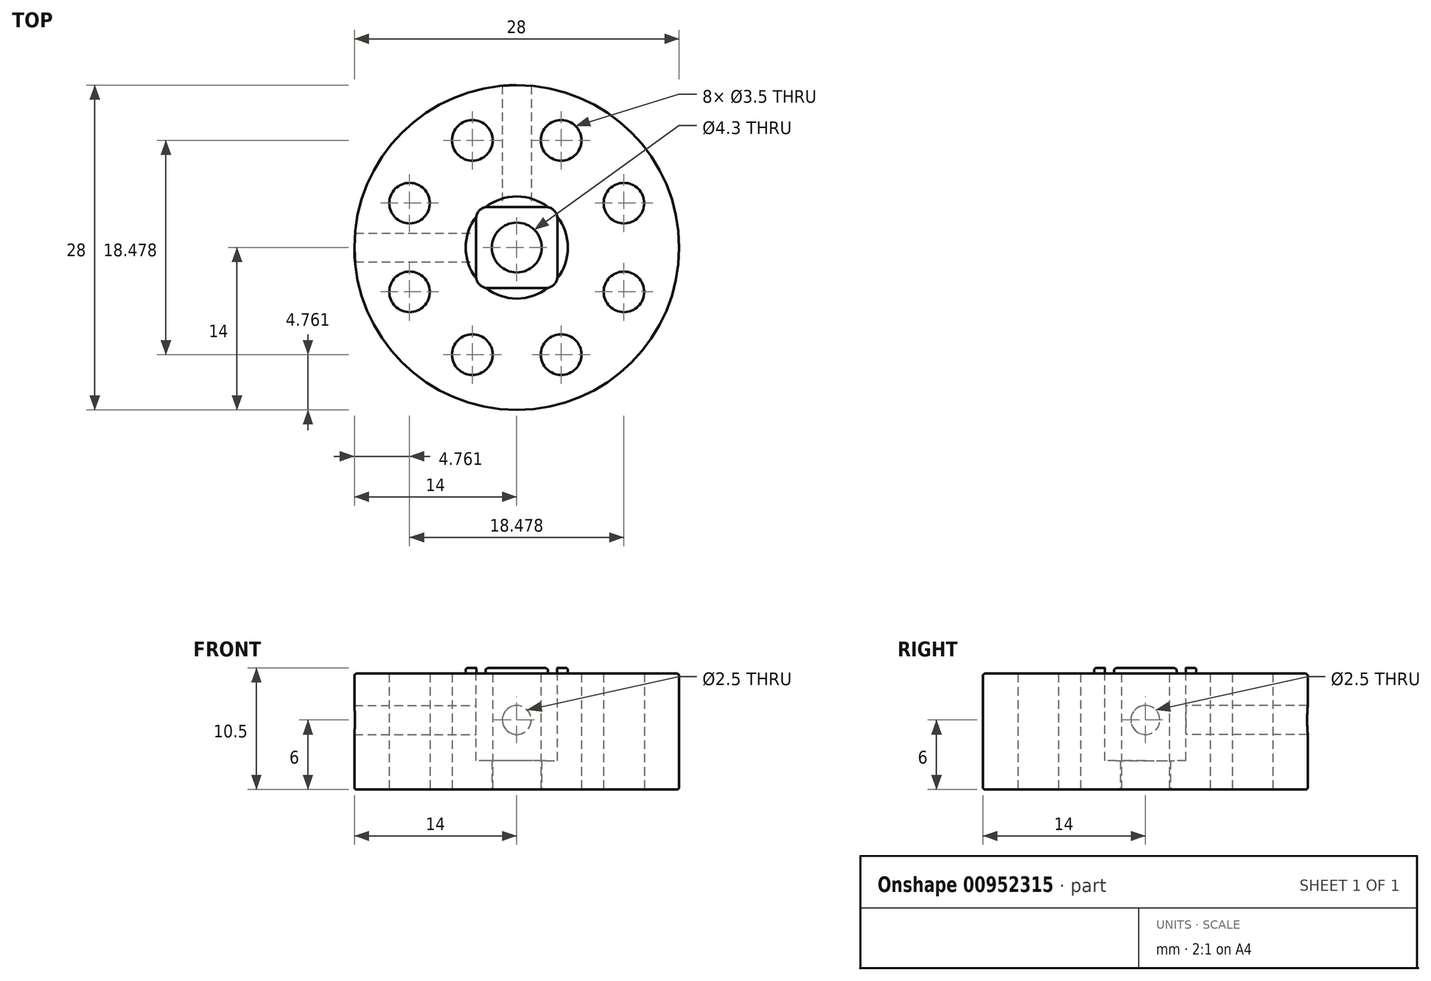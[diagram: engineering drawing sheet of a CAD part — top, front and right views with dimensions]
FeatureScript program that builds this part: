
annotation { "Feature Type Name" : "Feature", "Feature Type Description" : "" }
export const myFeature = defineFeature(function(context is Context, id is Id, definition is map)
    precondition{}
    {
        {
            var Q0;
            Q0=qCreatedBy(makeId("Top.planeOp"),FACE);
            var sketch = newSketch(context, id + "F0", { "sketchPlane" : qUnion([Q0])});
            skCircle(sketch, "E0", {"center": v(0, 0) * mm, "radius": 14 * mm});
            skSolve(sketch);
        }
        {
            var Q0;
            Q0=qSketchRegion(id+"F0",true);
            extrude(context, id + "F1", {"entities" : qUnion([Q0]), "depth" : 10 * mm, "offsetDistance" : 25 * mm});
        }
        {
            var Q0;
            Q0=makeQuery(id+"F1.opExtrude","CAP_FACE",FACE,{"disambiguationData":[OSD([sQuery(id+"F0.wireOp",EDGE,"E0")])],"isStart":false});
            var sketch = newSketch(context, id + "F2", { "sketchPlane" : qUnion([Q0])});
            skCircle(sketch, "E1", {"center": v(0, 0) * mm, "radius": 4.4 * mm});
            skSolve(sketch);
        }
        {
            var Q0;
            {var subQ0=sQuery(id+"F2.wireOp",EDGE,"q5Iyk92a-tP6P-DxR0-Fjeh-1lhmU1jtPTMJ");var subQ1=makeQuery(id+"F5.boolean.opBoolean","COPY",EDGE,{"derivedFrom":makeQuery(id+"F5.opExtrude","CAP_EDGE",EDGE,{"disambiguationData":[OSD([sQuery(id+"F4.wireOp",EDGE,"E2.bottom")])],"isStart":true})});var subQ2=makeQuery(id+"F2.imprint","INTERSECT",VERTEX,{"disambiguationData":[OD(0.0)],"derivedFrom":[subQ1,subQ0]});Q0=makeQuery(id+"F2.imprint","IMPRINT",FACE,{"disambiguationData":[TD([[makeQuery(id+"F2.imprint","IMPRINT",EDGE,{"disambiguationData":[TD([[subQ2,-1.0]])],"derivedFrom":subQ0}),1.0]])]});}
            var Q1;
            {var subQ0=sQuery(id+"F2.wireOp",EDGE,"q5Iyk92a-tP6P-DxR0-Fjeh-1lhmU1jtPTMJ");var subQ1=makeQuery(id+"F5.boolean.opBoolean","COPY",EDGE,{"derivedFrom":makeQuery(id+"F5.opExtrude","CAP_EDGE",EDGE,{"disambiguationData":[OSD([sQuery(id+"F4.wireOp",EDGE,"E2.right")])],"isStart":true})});var subQ2=makeQuery(id+"F2.imprint","INTERSECT",VERTEX,{"disambiguationData":[OD(0.0)],"derivedFrom":[subQ1,subQ0]});Q1=makeQuery(id+"F2.imprint","IMPRINT",FACE,{"disambiguationData":[TD([[makeQuery(id+"F2.imprint","IMPRINT",EDGE,{"disambiguationData":[TD([[subQ2,-1.0]])],"derivedFrom":subQ0}),1.0]])]});}
            var Q2;
            {var subQ0=sQuery(id+"F2.wireOp",EDGE,"q5Iyk92a-tP6P-DxR0-Fjeh-1lhmU1jtPTMJ");var subQ1=makeQuery(id+"F5.boolean.opBoolean","COPY",EDGE,{"derivedFrom":makeQuery(id+"F5.opExtrude","CAP_EDGE",EDGE,{"disambiguationData":[OSD([sQuery(id+"F4.wireOp",EDGE,"E2.top")])],"isStart":true})});var subQ2=makeQuery(id+"F2.imprint","INTERSECT",VERTEX,{"disambiguationData":[OD(0.0)],"derivedFrom":[subQ1,subQ0]});Q2=makeQuery(id+"F2.imprint","IMPRINT",FACE,{"disambiguationData":[TD([[makeQuery(id+"F2.imprint","IMPRINT",EDGE,{"disambiguationData":[TD([[subQ2,-1.0]])],"derivedFrom":subQ0}),1.0]])]});}
            var Q3;
            {var subQ0=sQuery(id+"F2.wireOp",EDGE,"q5Iyk92a-tP6P-DxR0-Fjeh-1lhmU1jtPTMJ");var subQ1=makeQuery(id+"F5.boolean.opBoolean","COPY",EDGE,{"derivedFrom":makeQuery(id+"F5.opExtrude","CAP_EDGE",EDGE,{"disambiguationData":[OSD([sQuery(id+"F4.wireOp",EDGE,"E2.left")])],"isStart":true})});var subQ2=makeQuery(id+"F2.imprint","INTERSECT",VERTEX,{"disambiguationData":[OD(0.0)],"derivedFrom":[subQ1,subQ0]});Q3=makeQuery(id+"F2.imprint","IMPRINT",FACE,{"disambiguationData":[TD([[makeQuery(id+"F2.imprint","IMPRINT",EDGE,{"disambiguationData":[TD([[subQ2,1.0]])],"derivedFrom":subQ0}),1.0]])]});}
            var Q4;
            Q4=makeQuery(id+"F2.imprint","IMPRINT",FACE,{"disambiguationData":[TD([[makeQuery(id+"F2.imprint","IMPRINT",EDGE,{"derivedFrom":sQuery(id+"F2.wireOp",EDGE,"E1")}),1.0]])]});
            extrude(context, id + "F3", {"entities" : qUnion([Q0, Q1, Q2, Q3, Q4]), "operationType" : NewBodyOperationType.ADD, "depth" : 0.5 * mm, "offsetDistance" : 25 * mm});
        }
        {
            var Q0;
            Q0=makeQuery(id+"F3.opExtrude","CAP_FACE",FACE,{"disambiguationData":[OSD([sQuery(id+"F2.wireOp",EDGE,"E1")])],"isStart":false});
            var sketch = newSketch(context, id + "F4", { "sketchPlane" : qUnion([Q0])});
            skLineSegment(sketch, "E2.bottom", {"start": v(3.5, -3.5) * mm, "end": v(-3.5, -3.5) * mm});
            skLineSegment(sketch, "E2.top", {"start": v(3.5, 3.5) * mm, "end": v(-3.5, 3.5) * mm});
            skLineSegment(sketch, "E2.left", {"start": v(3.5, -3.5) * mm, "end": v(3.5, 3.5) * mm});
            skLineSegment(sketch, "E2.right", {"start": v(-3.5, -3.5) * mm, "end": v(-3.5, 3.5) * mm});
            skPoint(sketch, "E2.middle", {"position": v(0, 0) * mm});
            skSolve(sketch);
        }
        {
            var Q0;
            Q0=qSketchRegion(id+"F4",true);
            extrude(context, id + "F5", {"entities" : qUnion([Q0]), "operationType" : NewBodyOperationType.REMOVE, "oppositeDirection" : true, "depth" : 8 * mm, "offsetDistance" : 25 * mm});
        }
        {
            var Q0;
            Q0=makeQuery(id+"F1.opExtrude","CAP_FACE",FACE,{"disambiguationData":[OSD([sQuery(id+"F0.wireOp",EDGE,"E0")])],"isStart":true});
            var sketch = newSketch(context, id + "F6", { "sketchPlane" : qUnion([Q0])});
            skCircle(sketch, "E3", {"center": v(0, 0) * mm, "radius": 2.15 * mm});
            skSolve(sketch);
        }
        {
            var Q0;
            Q0=qSketchRegion(id+"F6",true);
            var Q1;
            Q1=makeQuery(id+"F5.boolean.opBoolean","COPY",FACE,{"derivedFrom":makeQuery(id+"F5.opExtrude","CAP_FACE",FACE,{"disambiguationData":[OSD([sQuery(id+"F4.wireOp",EDGE,"E2.bottom"),sQuery(id+"F4.wireOp",EDGE,"E2.top"),sQuery(id+"F4.wireOp",EDGE,"E2.left"),sQuery(id+"F4.wireOp",EDGE,"E2.right")])],"isStart":false})});
            extrude(context, id + "F7", {"entities" : qUnion([Q0]), "operationType" : NewBodyOperationType.REMOVE, "endBound" : BoundingType.UP_TO_SURFACE, "oppositeDirection" : true, "depth" : 25 * mm, "endBoundEntityFace" : qUnion([Q1]), "offsetDistance" : 25 * mm});
        }
        {
            var Q0;
            Q0=makeQuery(id+"F1.opExtrude","CAP_FACE",FACE,{"disambiguationData":[OSD([sQuery(id+"F0.wireOp",EDGE,"E0")])],"isStart":true});
            var sketch = newSketch(context, id + "F8", { "sketchPlane" : qUnion([Q0])});
            skCircle(sketch, "E4", {"center": v(9.24, 3.83) * mm, "radius": 1.75 * mm});
            skCircle(sketch, "E5.1.0", {"center": v(3.83, 9.24) * mm, "radius": 1.75 * mm});
            skCircle(sketch, "E5.2.0", {"center": v(-3.83, 9.24) * mm, "radius": 1.75 * mm});
            skCircle(sketch, "E5.3.0", {"center": v(-9.24, 3.83) * mm, "radius": 1.75 * mm});
            skCircle(sketch, "E5.4.0", {"center": v(-9.24, -3.83) * mm, "radius": 1.75 * mm});
            skCircle(sketch, "E5.5.0", {"center": v(-3.83, -9.24) * mm, "radius": 1.75 * mm});
            skCircle(sketch, "E5.6.0", {"center": v(3.83, -9.24) * mm, "radius": 1.75 * mm});
            skCircle(sketch, "E5.7.0", {"center": v(9.24, -3.83) * mm, "radius": 1.75 * mm});
            skPoint(sketch, "E5.center", {"position": v(0, 0) * mm});
            skLineSegment(sketch, "E6", {"start": v(9.24, 3.83) * mm, "end": v(0, 0) * mm});
            skSolve(sketch);
        }
        {
            var Q0;
            Q0=qSketchRegion(id+"F8",true);
            var Q1;
            Q1=makeQuery(id+"F1.opExtrude","CAP_FACE",FACE,{"disambiguationData":[OSD([sQuery(id+"F0.wireOp",EDGE,"E0")])],"isStart":false});
            extrude(context, id + "F9", {"entities" : qUnion([Q0]), "operationType" : NewBodyOperationType.REMOVE, "endBound" : BoundingType.UP_TO_SURFACE, "oppositeDirection" : true, "depth" : 25 * mm, "endBoundEntityFace" : qUnion([Q1]), "offsetDistance" : 25 * mm});
        }
        {
            var Q0;
            Q0=qCreatedBy(makeId("Front.planeOp"),FACE);
            var sketch = newSketch(context, id + "F10", { "sketchPlane" : qUnion([Q0])});
            skCircle(sketch, "E7", {"center": v(0, 6) * mm, "radius": 1.25 * mm});
            skSolve(sketch);
        }
        {
            var Q0;
            Q0=qSketchRegion(id+"F10",true);
            extrude(context, id + "F11", {"entities" : qUnion([Q0]), "operationType" : NewBodyOperationType.REMOVE, "oppositeDirection" : true, "depth" : 25 * mm, "offsetDistance" : 25 * mm});
        }
        {
            var Q0;
            Q0=qCreatedBy(makeId("Right.planeOp"),FACE);
            var sketch = newSketch(context, id + "F12", { "sketchPlane" : qUnion([Q0])});
            skCircle(sketch, "E8", {"center": v(0, 6) * mm, "radius": 1.25 * mm});
            skSolve(sketch);
        }
        {
            var Q0;
            Q0=qSketchRegion(id+"F12",true);
            extrude(context, id + "F13", {"entities" : qUnion([Q0]), "operationType" : NewBodyOperationType.REMOVE, "oppositeDirection" : true, "depth" : 25 * mm, "offsetDistance" : 25 * mm});
        }
        {
            var Q0;
            {var subQ0=sQuery(id+"F4.wireOp",EDGE,"E2.right");var subQ1=sQuery(id+"F4.wireOp",EDGE,"E2.bottom");Q0=makeQuery(id+"F3.boolean.opBoolean","MERGE",EDGE,{"derivedFrom":[makeQuery(id+"F5.boolean.opBoolean","COPY",EDGE,{"derivedFrom":makeQuery(id+"F5.opExtrude","SWEPT_EDGE",EDGE,{"disambiguationData":[OSD([subQ1,subQ0])]})}),makeQuery(id+"F3.opExtrude","SWEPT_EDGE",EDGE,{"disambiguationData":[OSD([subQ1,subQ0])]})]});}
            var Q1;
            {var subQ0=sQuery(id+"F4.wireOp",EDGE,"E2.left");var subQ1=sQuery(id+"F4.wireOp",EDGE,"E2.bottom");Q1=makeQuery(id+"F3.boolean.opBoolean","MERGE",EDGE,{"derivedFrom":[makeQuery(id+"F5.boolean.opBoolean","COPY",EDGE,{"derivedFrom":makeQuery(id+"F5.opExtrude","SWEPT_EDGE",EDGE,{"disambiguationData":[OSD([subQ1,subQ0])]})}),makeQuery(id+"F3.opExtrude","SWEPT_EDGE",EDGE,{"disambiguationData":[OSD([subQ1,subQ0])]})]});}
            var Q2;
            {var subQ0=sQuery(id+"F4.wireOp",EDGE,"E2.left");var subQ1=sQuery(id+"F4.wireOp",EDGE,"E2.top");Q2=makeQuery(id+"F3.boolean.opBoolean","MERGE",EDGE,{"derivedFrom":[makeQuery(id+"F5.boolean.opBoolean","COPY",EDGE,{"derivedFrom":makeQuery(id+"F5.opExtrude","SWEPT_EDGE",EDGE,{"disambiguationData":[OSD([subQ1,subQ0])]})}),makeQuery(id+"F3.opExtrude","SWEPT_EDGE",EDGE,{"disambiguationData":[OSD([subQ1,subQ0])]})]});}
            var Q3;
            {var subQ0=sQuery(id+"F4.wireOp",EDGE,"E2.right");var subQ1=sQuery(id+"F4.wireOp",EDGE,"E2.top");Q3=makeQuery(id+"F3.boolean.opBoolean","MERGE",EDGE,{"derivedFrom":[makeQuery(id+"F5.boolean.opBoolean","COPY",EDGE,{"derivedFrom":makeQuery(id+"F5.opExtrude","SWEPT_EDGE",EDGE,{"disambiguationData":[OSD([subQ1,subQ0])]})}),makeQuery(id+"F3.opExtrude","SWEPT_EDGE",EDGE,{"disambiguationData":[OSD([subQ1,subQ0])]})]});}
            fillet(context, id + "F14", {"entities" : qUnion([Q0, Q1, Q2, Q3]), "radius" : 1 * mm, "tangentPropagation" : true, "allowEdgeOverflow" : false});
        }
        {
            var Q0;
            Q0=makeQuery(id+"F1.opExtrude","CAP_EDGE",EDGE,{"disambiguationData":[OSD([sQuery(id+"F0.wireOp",EDGE,"E0")])],"isStart":false});
            var Q1;
            Q1=makeQuery(id+"F1.opExtrude","CAP_EDGE",EDGE,{"disambiguationData":[OSD([sQuery(id+"F0.wireOp",EDGE,"E0")])],"isStart":true});
            var Q2;
            Q2=makeQuery(id+"F3.opExtrude","CAP_EDGE",EDGE,{"disambiguationData":[OSD([sQuery(id+"F2.wireOp",EDGE,"E1")])],"isStart":false});
            var Q3;
            Q3=makeQuery(id+"F3.opExtrude","CAP_EDGE",EDGE,{"disambiguationData":[OSD([sQuery(id+"F4.wireOp",EDGE,"E2.bottom")])],"isStart":false});
            fillet(context, id + "F15", {"entities" : qUnion([Q0, Q1, Q2, Q3]), "radius" : 0.2 * mm, "tangentPropagation" : true, "allowEdgeOverflow" : false});
        }
    });
